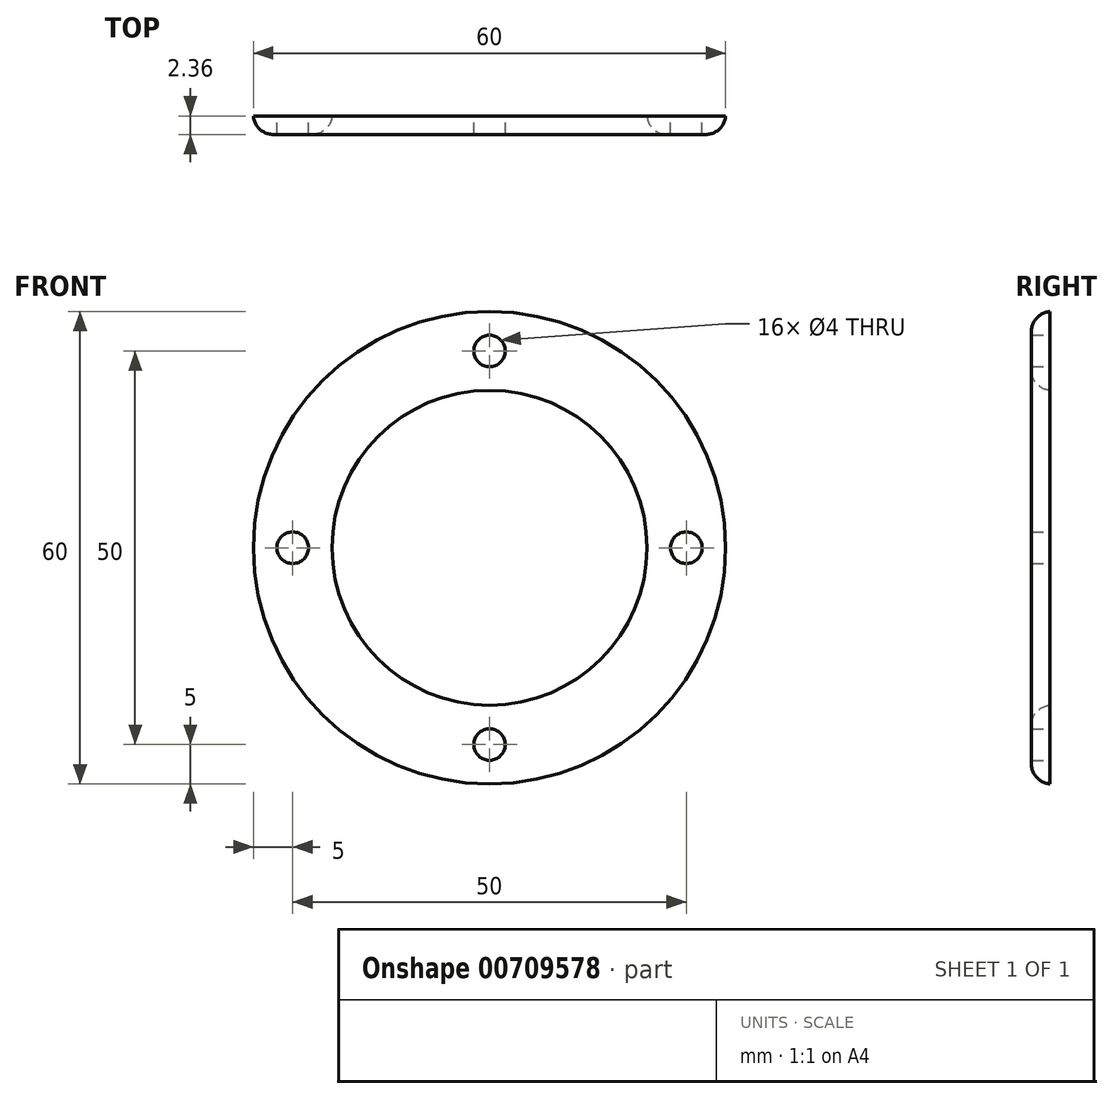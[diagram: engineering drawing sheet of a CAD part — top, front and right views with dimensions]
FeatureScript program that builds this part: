
annotation { "Feature Type Name" : "Feature", "Feature Type Description" : "" }
export const myFeature = defineFeature(function(context is Context, id is Id, definition is map)
    precondition{}
    {
        {
            var Q0;
            Q0=qCreatedBy(makeId("Front.planeOp"),FACE);
            var sketch = newSketch(context, id + "F0", { "sketchPlane" : qUnion([Q0])});
            skCircle(sketch, "E0", {"center": v(0, 0) * mm, "radius": 16 * mm});
            skCircle(sketch, "E1", {"center": v(0, 0) * mm, "radius": 20 * mm});
            skCircle(sketch, "E2", {"center": v(0, 0) * mm, "radius": 30 * mm});
            skLineSegment(sketch, "E3", {"start": v(-20, 0) * mm, "end": v(-20, 22.36) * mm});
            skLineSegment(sketch, "E4", {"start": v(-16, 0) * mm, "end": v(-16, 25.38) * mm});
            skLineSegment(sketch, "E5", {"start": v(20, 0) * mm, "end": v(20, 22.36) * mm});
            skLineSegment(sketch, "E6", {"start": v(16, 0) * mm, "end": v(16, 25.38) * mm});
            skCircle(sketch, "E7", {"center": v(-25, 0) * mm, "radius": 2 * mm});
            skCircle(sketch, "E8", {"center": v(0, -25) * mm, "radius": 2 * mm});
            skCircle(sketch, "E9", {"center": v(25, 0) * mm, "radius": 2 * mm});
            skCircle(sketch, "E10", {"center": v(0, 25) * mm, "radius": 2 * mm});
            skSolve(sketch);
        }
        {
            var Q0;
            {var subQ1=sQuery(id+"F0.wireOp",EDGE,"E3");Q0=makeQuery(id+"F0.imprint","IMPRINT",FACE,{"disambiguationData":[TD([[makeQuery(id+"F0.imprint","IMPRINT",EDGE,{"derivedFrom":subQ1}),1.0]])]});}
            var Q1;
            Q1=makeQuery(id+"F0.imprint","IMPRINT",FACE,{"disambiguationData":[TD([[makeQuery(id+"F0.imprint","IMPRINT",EDGE,{"derivedFrom":sQuery(id+"F0.wireOp",EDGE,"E10")}),-1.0]])]});
            var Q2;
            {var subQ0=sQuery(id+"F0.wireOp",EDGE,"E5");Q2=makeQuery(id+"F0.imprint","IMPRINT",FACE,{"disambiguationData":[TD([[makeQuery(id+"F0.imprint","IMPRINT",EDGE,{"derivedFrom":subQ0}),1.0]])]});}
            var Q3;
            {var subQ0=sQuery(id+"F0.wireOp",EDGE,"E3");Q3=makeQuery(id+"F0.imprint","IMPRINT",FACE,{"disambiguationData":[TD([[makeQuery(id+"F0.imprint","IMPRINT",EDGE,{"derivedFrom":subQ0}),-1.0]])]});}
            extrude(context, id + "F1", {"entities" : qUnion([Q0, Q1, Q2, Q3]), "depth" : 2.36 * mm, "offsetDistance" : 25.4 * mm});
        }
        {
            var Q0;
            {var subQ0=sQuery(id+"F0.wireOp",EDGE,"E2");Q0=makeQuery(id+"F1.opExtrude","CAP_EDGE",EDGE,{"disambiguationData":[OSD([subQ0]),TDD([makeQuery(id+"F0.imprint","IMPRINT",EDGE,{"disambiguationData":[TD([[makeQuery(id+"F0.imprint","INTERSECT",VERTEX,{"derivedFrom":[subQ0,sQuery(id+"F0.wireOp",EDGE,"E3")]}),-1.0]])],"derivedFrom":subQ0})])],"isStart":false});}
            var Q1;
            {var subQ0=sQuery(id+"F0.wireOp",EDGE,"E2");Q1=makeQuery(id+"F1.opExtrude","CAP_EDGE",EDGE,{"disambiguationData":[OSD([subQ0]),TDD([makeQuery(id+"F0.imprint","IMPRINT",EDGE,{"disambiguationData":[TD([[makeQuery(id+"F0.imprint","INTERSECT",VERTEX,{"derivedFrom":[subQ0,sQuery(id+"F0.wireOp",EDGE,"E4")]}),1.0]])],"derivedFrom":subQ0})])],"isStart":false});}
            var Q2;
            Q2=makeQuery(id+"F1.opExtrude","CAP_EDGE",EDGE,{"disambiguationData":[OSD([sQuery(id+"F0.wireOp",EDGE,"E1")])],"isStart":false});
            fillet(context, id + "F2", {"entities" : qUnion([Q0, Q1, Q2]), "radius" : 2.54 * mm, "tangentPropagation" : true, "allowEdgeOverflow" : false});
        }
    });
